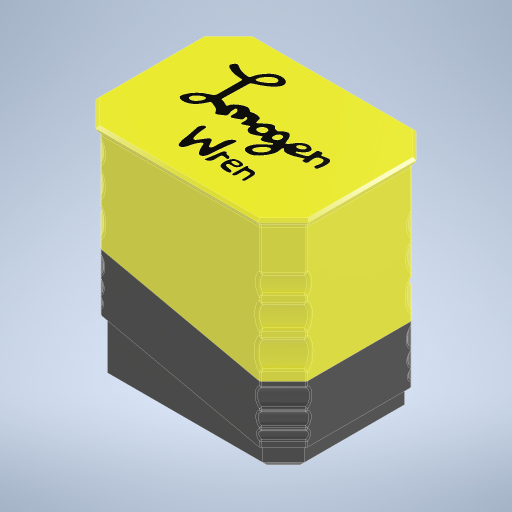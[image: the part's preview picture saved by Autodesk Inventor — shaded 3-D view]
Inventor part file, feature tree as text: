
AUTODESK INVENTOR PART (.ipt)
format: ipt  version: 2024.1 (Build 281209000, 209)  size: 3,311,616 bytes
history: native  units: mm
features: sketch x36, projected_geometry x35, extrude x33, chamfer x20, fillet x16, plane x5, other x4, sweep x1, revolve x1, pattern_linear x1
ambient origin geometry x8: Origin, YZ Plane, XZ Plane, XY Plane, X Axis, Y Axis, Z Axis, Center Point
bodies: Body1 (feature_tree), Body2 (feature_tree), Body3 (feature_tree)
feature tree (152):
  other  "transmitter"
  extrude  "Extrusion1"  Depth=90.6mm
  sweep  "Sweep2"
  chamfer  "Chamfer1"  Distance=14.0mm
  chamfer  "Chamfer2"  [1 undecoded]
  chamfer  "Chamfer3"  Distance=80.0mm Angle=45.0deg
  chamfer  "Chamfer4"  Distance=1.0mm Angle=45.0deg
  chamfer  "Chamfer5"  Distance=9.5mm Angle=45.0deg
  chamfer  "Chamfer6"  Distance=1.0mm Angle=45.0deg
  chamfer  "Chamfer7"  Distance=1.0mm Angle=45.0deg
  extrude  "Extrusion2"  Depth=1.0mm TaperAngle=45.0deg
  extrude  "Extrusion3"  Depth=24.3mm
  plane  "Work Plane1"
  revolve  "Revolution1"  [1 undecoded]
  fillet  "Fillet1"  Radius=13.5mm
  fillet  "Fillet2"  Radius=24.22mm
  fillet  "Fillet3"  Radius=3.175mm
  fillet  "Fillet4"  Radius=2.05mm
  extrude  "Extrusion5"  Depth=2.3mm
  fillet  "Fillet5"  Radius=3.06mm
  extrude  "Extrusion6"  Depth=0.853mm
  extrude  "Extrusion7"  Depth=0.5mm
  pattern_linear  "Rectangular Pattern1"  Count1=2 Spacing1=28.0mm
  extrude  "Extrusion9"  Depth=7.0mm
  extrude  "Extrusion10"  Depth=3.0mm
  extrude  "Extrusion11"  Depth=2.0mm
  extrude  "Extrusion12"  Depth=61.5mm TaperAngle=0.0deg
  chamfer  "Chamfer9"  Distance=30.0mm
  chamfer  "Chamfer10"  Distance=3.0mm
  extrude  "Extrusion13"  Depth=10.0mm
  extrude  "Extrusion17"  Depth=10.0mm
  extrude  "Extrusion18"  Depth=10.0mm
  extrude  "Extrusion19"  Depth=10.0mm
  extrude  "Extrusion14"  Depth=10.0mm
  extrude  "Extrusion20"  Depth=10.0mm
  extrude  "Extrusion21"  Depth=10.0mm
  extrude  "Extrusion22"  Depth=10.0mm
  extrude  "Extrusion15"  Depth=1.6mm TaperAngle=0.0deg
  extrude  "Extrusion23"  Depth=1.6mm TaperAngle=0.0deg
  extrude  "Extrusion24"  Depth=10.0mm TaperAngle=45.0deg
  extrude  "Extrusion25"  Depth=10.0mm TaperAngle=45.0deg
  chamfer  "Chamfer11"  Distance=2.0mm
  extrude  "Extrusion26"  Depth=1.6mm TaperAngle=0.0deg
  extrude  "Extrusion27"  Depth=1.6mm TaperAngle=0.0deg
  chamfer  "Chamfer12"  Distance=4.0mm
  fillet  "Fillet6"  Radius=54.12mm
  fillet  "Fillet7"  Radius=15.0mm
  fillet  "Fillet8"  Radius=15.0mm
  plane  "Work Plane3"
  plane  "Work Plane4"
  sketch  "Sketch37"  dims[d74=21.5mm d75=0.0mm]
  extrude  "Extrusion28"  Depth=10.0mm TaperAngle=0.0deg
  extrude  "Extrusion29"  Depth=10.0mm TaperAngle=0.0deg
  plane  "Work Plane5"
  plane  "Work Plane6"
  extrude  "Extrusion32"  Depth=10.0mm TaperAngle=0.0deg
  extrude  "Extrusion30"  Depth=10.0mm TaperAngle=0.0deg
  extrude  "Extrusion31"  Depth=10.0mm TaperAngle=0.0deg
  extrude  "Extrusion33"  Depth=10.0mm TaperAngle=0.0deg
  chamfer  "Chamfer13"  Distance=10.0mm
  chamfer  "Chamfer14"  Distance=3.0mm Angle=45.0deg
  extrude  "Extrusion34"  Depth=1.6mm TaperAngle=0.0deg
  fillet  "Fillet9"  Radius=1.5mm
  fillet  "Fillet10"  Radius=2.5mm
  chamfer  "Chamfer15"  Distance=1.0mm Angle=45.0deg
  chamfer  "Chamfer16"  Distance=1.5mm
  fillet  "Fillet11"  Radius=2.0mm
  fillet  "Fillet12"  Radius=1.0mm
  chamfer  "Chamfer17"  Distance=6.0mm
  extrude  "Extrusion35"  Depth=10.0mm
  fillet  "Fillet13"  Radius=1.8mm
  chamfer  "Chamfer18"  Distance=5.0mm
  fillet  "Fillet14"  Radius=14.0mm
  fillet  "Fillet15"  Radius=1.6mm
  chamfer  "Chamfer19"  Distance=12.0mm
  chamfer  "Chamfer20"  Distance=1.4mm
  chamfer  "Chamfer21"  Distance=4.0mm
  fillet  "Fillet16"  Radius=6.0mm
  extrude  "Extrusion36"  Depth=1.6mm
  sketch  "Sketch1"  dims[d0=43.3mm d1=90.6mm]
  sketch  "Sketch2"  dims[d2=43.3mm d3=6.3mm]
  sketch  "Sketch3"  dims[d4=8.0mm]
  projected_geometry  "Projected Loop1"
  sketch  "Sketch4"  dims[d5=6.5mm]
  sketch  "Sketch5"  dims[d6=7.8mm d7=14.0mm d8=0.0mm]
  other  "Work Point1"
  sketch  "Sketch7"  dims[d9=1.85mm]
  sketch  "Sketch8"  dims[d10=1.85mm]
  sketch  "Sketch9"  dims[d11=10.3mm d14=0.0mm d15=0.0mm d16=80.0mm d17=1.0mm d18=45.0deg d19=1.0mm d20=80.0mm d21=45.0deg d22=9.5mm d23=80.0mm d24=45.0deg d25=1.0mm d26=80.0mm d27=45.0deg d28=1.0mm d29=80.0mm d30=45.0deg]
  sketch  "Sketch10"  dims[d31=1.0mm d32=12.0mm d33=45.0deg d34=1.0mm d35=12.0mm d36=45.0deg]
  sketch  "Sketch13"  dims[d37=11.2mm d38=24.3mm]
  other  "body-case"
  sketch  "Sketch14"  dims[d39=14.7mm d40=0.0mm d41=12.26mm d42=13.5mm d43=0.0mm d50=24.22mm d51=3.175mm d52=2.05mm]
  projected_geometry  "Projected Loop15"
  projected_geometry  "Projected Loop16"
  projected_geometry  "Projected Loop17"
  projected_geometry  "Projected Loop18"
  projected_geometry  "Projected Loop19"
  projected_geometry  "Projected Loop20"
  projected_geometry  "Projected Loop21"
  projected_geometry  "Projected Loop22"
  sketch  "Sketch15"  dims[d53=1.38mm d54=2.3mm d55=3.06mm]
  projected_geometry  "Projected Loop23"
  sketch  "Sketch16"  dims[d56=3.54mm d57=0.853mm]
  projected_geometry  "Projected Loop24"
  sketch  "Sketch17"  dims[d58=90.0deg d59=0.5mm]
  projected_geometry  "Projected Loop25"
  sketch  "Sketch18"  dims[d60=0.8mm]
  projected_geometry  "Projected Loop26"
  sketch  "Sketch20"  dims[d61=0.8mm]
  projected_geometry  "Projected Loop27"
  other  "lid"
  sketch  "Sketch22"  dims[d62=0.8mm]
  projected_geometry  "Projected Loop29"
  projected_geometry  "Projected Loop30"
  sketch  "Sketch24"  dims[d63=6.8mm]
  projected_geometry  "Projected Loop31"
  sketch  "Sketch26"  dims[d64=10.1mm]
  projected_geometry  "Projected Loop32"
  sketch  "Sketch27"  dims[d65=4.3mm]
  projected_geometry  "Projected Loop33"
  sketch  "Sketch28"  dims[d66=18.5mm]
  projected_geometry  "Projected Loop34"
  projected_geometry  "Projected Loop35"
  projected_geometry  "Projected Loop36"
  projected_geometry  "Projected Loop37"
  sketch  "Sketch29"  dims[d67=30.6mm]
  projected_geometry  "Projected Loop38"
  sketch  "Sketch30"  dims[d68=1.6mm d69=0.0mm]
  projected_geometry  "Projected Loop39"
  sketch  "Sketch31"  dims[d70=0.8mm]
  projected_geometry  "Projected Loop40"
  projected_geometry  "Projected Loop41"
  projected_geometry  "Projected Loop42"
  projected_geometry  "Projected Loop43"
  sketch  "Sketch32"  dims[d71=5.5mm]
  projected_geometry  "Projected Loop44"
  sketch  "Sketch34"  dims[d72=10.5mm]
  projected_geometry  "Projected Loop45"
  sketch  "Sketch35"  dims[d73=2.8mm]
  projected_geometry  "Projected Loop46"
  sketch  "Sketch38"  dims[d76=3.2mm]
  sketch  "Sketch39"  dims[d77=10.0mm d78=0.0mm d79=20.0mm d81=28.0mm]
  sketch  "Sketch40"  dims[d88=7.0mm d89=7.0mm]
  sketch  "Sketch41"  dims[d90=8.0mm d91=3.0mm]
  sketch  "Sketch42"  dims[d92=3.0mm d93=0.0mm d94=2.0mm]
  projected_geometry  "Projected Loop47"
  sketch  "Sketch44"  dims[d96=2.0mm d97=61.5mm d98=0.0mm]
  projected_geometry  "Projected Loop48"
  sketch  "Sketch45"  dims[d100=4.0mm]
  sketch  "Sketch46"  dims[d101=4.0mm d102=30.0mm d103=3.0mm d104=10.0mm d105=10.0mm d106=10.0mm d107=10.0mm d108=10.0mm d109=10.0mm d110=10.0mm d111=10.0mm d112=61.5mm d113=0.0mm d114=3.0mm d115=0.0mm d116=10.0mm d117=2.0mm d118=45.0deg d119=10.0mm d120=2.0mm d121=45.0deg d122=2.0mm d123=15.0mm d124=0.0mm d125=25.0mm d126=0.0mm d127=4.0mm d128=54.12mm d129=0.0mm d133=15.0mm d134=0.0mm d135=15.0mm d136=0.0mm d137=10.0mm d138=0.0mm d139=10.0mm d140=0.0mm d141=10.0mm d142=0.0mm d143=10.0mm d144=0.0mm d145=10.0mm d146=0.0mm d147=10.0mm d148=0.0mm d149=10.0mm d150=0.0mm d151=3.0mm d152=2.0mm d153=45.0deg d154=2.0mm d155=0.0mm d156=1.5mm d157=2.5mm d158=0.0mm d159=1.0mm d160=2.0mm d161=45.0deg d162=1.5mm d163=2.0mm d164=1.0mm d165=6.0mm d166=10.0mm d167=1.8mm d168=5.0mm d169=14.0mm d170=1.6mm d171=12.0mm d172=1.4mm d173=4.0mm d174=6.0mm d175=4.0mm d176=1.8mm d177=3.0mm d178=8.0mm d179=6.0mm d180=1.6mm d181=1.4mm d182=2.0mm d183=0.0mm d184=0.0mm d185=6.0mm d186=10.0mm d187=1.8mm d188=5.0mm d189=14.0mm d190=1.6mm d191=12.0mm d192=1.4mm d193=4.0mm d194=6.0mm d195=4.0mm d196=1.8mm d197=3.0mm d198=8.0mm d199=6.0mm d200=1.6mm d201=1.4mm d202=2.0mm d203=0.0mm d204=0.0mm d205=6.0mm d206=10.0mm d207=1.8mm d208=5.0mm d209=14.0mm d210=1.6mm d211=12.0mm d212=1.4mm d213=4.0mm d214=6.0mm d215=4.0mm d216=1.8mm d217=3.0mm d218=8.0mm d219=6.0mm d220=1.6mm d221=1.4mm d222=2.0mm d223=0.0mm d224=0.0mm d225=6.0mm d226=10.0mm d227=1.8mm d228=5.0mm d229=14.0mm d230=1.6mm d231=12.0mm d232=1.4mm d233=4.0mm d234=6.0mm d235=4.0mm d236=1.8mm d237=3.0mm d238=8.0mm d239=6.0mm d240=1.6mm d241=1.4mm d242=2.0mm d243=0.0mm d244=0.0mm d245=0.02mm d246=0.0mm d247=0.35mm d248=0.35mm d249=0.02mm d250=0.0mm d251=1.5mm d252=2.0mm d253=45.0deg d254=3.0mm d255=2.0mm d256=45.0deg d257=2.0mm d258=2.0mm d259=1.0mm d260=0.0mm d261=2.0mm d262=2.0mm d263=45.0deg d264=2.0mm d265=2.0mm d266=45.0deg d267=1.0mm d268=1.0mm d269=3.0mm d270=2.0mm d271=45.0deg d272=24.0mm d273=10.15mm d274=9.85mm d275=4.0mm d276=4.0mm d277=43.0mm d278=0.0mm d279=2.0mm d280=1.9mm d281=2.0mm d282=45.0deg d283=2.1mm d284=2.1mm d285=0.5mm d286=2.0mm d287=45.0deg d288=2.0mm d289=2.0mm d290=45.0deg d291=2.0mm d292=2.0mm d293=45.0deg d294=2.0mm d295=1.0mm d296=27.0mm d297=0.0mm d298=0.7mm d299=0.7mm d300=0.7mm d301=0.7mm]
  projected_geometry  "Projected Loop49"
note: 2 required parameter values undecoded (feature->parameter linkage not recoverable at this tier; creation-order binding heuristic only, values carry confidence <= 0.55)